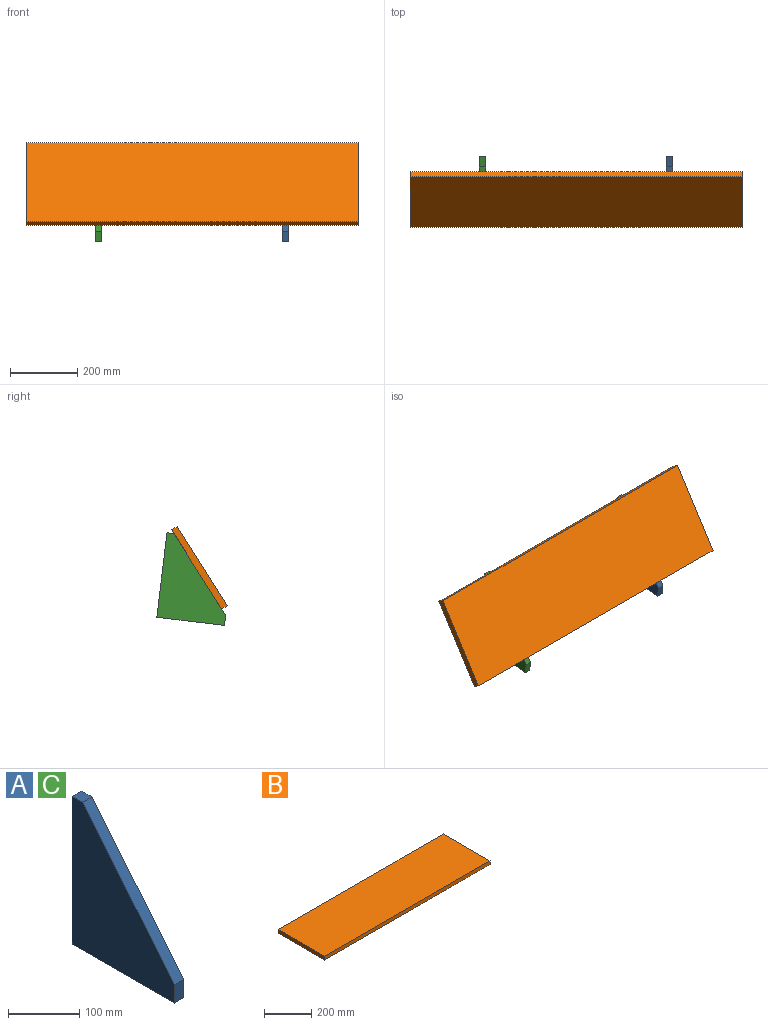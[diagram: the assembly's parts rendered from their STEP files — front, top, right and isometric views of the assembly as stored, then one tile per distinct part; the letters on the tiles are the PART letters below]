
ASSEMBLY  parts=3 mates=2
PART A: 7 faces, bbox 19.1x203.2x254 mm
  f0: plane 20.78x19.05mm, normal (0,0,1), area 395.9mm2, adj f1,f4,f5,f6
  f1: plane 222.96x182.42mm, normal (0,-0.77,0.63), area 5487.8mm2, adj f0,f2,f5,f6
  f2: plane 31.04x19.05mm, normal (0,-1,0), area 591.4mm2, adj f1,f3,f5,f6
  f3: plane 203.2x19.05mm, normal (0,0,-1), area 3871mm2, adj f2,f4,f5,f6
  f4: plane 254x19.05mm, normal (0,1,0), area 4838.7mm2, adj f0,f3,f5,f6
  f5: plane 254x203.2mm, normal (1,0,0), area 31277.2mm2, adj f0,f1,f2,f3,f4
  f6: plane 254x203.2mm, normal (-1,0,0), area 31277.2mm2, adj f0,f1,f2,f3,f4
PART B: 6 faces, bbox 990.6x279.4x19.1 mm
  f0: plane 990.6x19.05mm, normal (0,-1,0), area 18870.9mm2, adj f1,f3,f4,f5
  f1: plane 279.4x19.05mm, normal (1,0,0), area 5322.6mm2, adj f0,f2,f4,f5
  f2: plane 990.6x19.05mm, normal (0,1,0), area 18870.9mm2, adj f1,f3,f4,f5
  f3: plane 279.4x19.05mm, normal (-1,0,0), area 5322.6mm2, adj f0,f2,f4,f5
  f4: plane 990.6x279.4mm, normal (0,0,1), area 276773.6mm2, adj f0,f1,f2,f3
  f5: plane 990.6x279.4mm, normal (0,0,-1), area 276773.6mm2, adj f0,f1,f2,f3
PART C: same geometry as A
PLACE A rot(axis=(1,0,0),6.9deg) t=(-639.72,-7.7,247.4)mm
PLACE B rot(axis=(1,0,0),57.6deg) t=(-909.59,3.37,264.87)mm
PLACE C rot(axis=(1,0,0),6.9deg) t=(-1198.52,-7.7,247.4)mm
MATE planar B.f5 <-> C.f1  axis (0,0.84,-0.54) through (-909.59,3.37,264.87)mm
MATE planar B.f5 <-> A.f1  axis (0,0.84,-0.54) through (-909.59,3.37,264.87)mm
